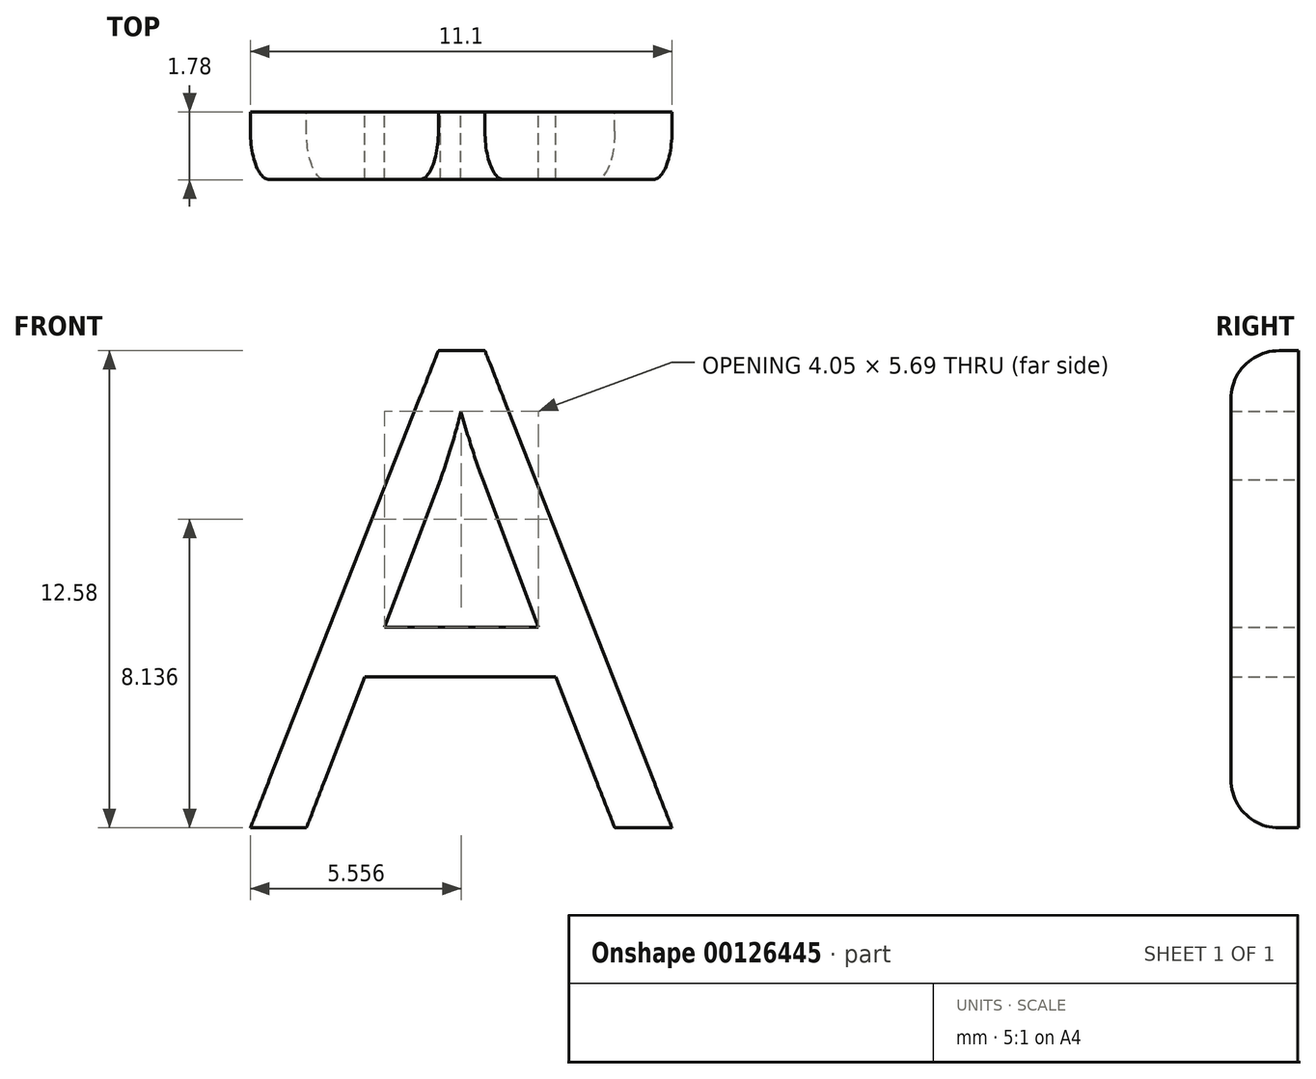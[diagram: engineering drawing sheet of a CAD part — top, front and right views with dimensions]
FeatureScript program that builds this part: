
annotation { "Feature Type Name" : "Feature", "Feature Type Description" : "" }
export const myFeature = defineFeature(function(context is Context, id is Id, definition is map)
    precondition{}
    {
        {
            var Q0;
            Q0=qCreatedBy(makeId("Front.planeOp"),FACE);
            var sketch = newSketch(context, id + "F0", { "sketchPlane" : qUnion([Q0])});
            skText(sketch, "E0", { "text": "A", "fontName": "OpenSans-Regular.ttf"});
            const initialGuessF0  = {"E0": [-0.00578, -0.00825, 1, 0, 0.01263]};
            skSetInitialGuess(sketch, initialGuessF0);
            skSolve(sketch);
        }
        {
            var Q0;
            Q0 = qSketchRegion(id + "F0", true);
            var Q1;
            Q1=makeQuery(id+"F0.imprint","IMPRINT",FACE,{"disambiguationData":[TD([[makeQuery(id+"F0.imprint","IMPRINT",EDGE,{"derivedFrom":sQuery(id+"F0.wireOp",EDGE,"E0.sketch_text.stroke-0")}),-1.0]])]});
            extrude(context, id + "F1", {"entities" : qUnion([Q0, Q1]), "depth" : 1.78 * mm});
        }
        {
            var Q0;
            Q0=makeQuery(id+"F1.opExtrude","CAP_EDGE",EDGE,{"disambiguationData":[OSD([sQuery(id+"F0.wireOp",EDGE,"E0.sketch_text.stroke-5")])],"isStart":false});
            var Q1;
            Q1=makeQuery(id+"F1.opExtrude","CAP_EDGE",EDGE,{"disambiguationData":[OSD([sQuery(id+"F0.wireOp",EDGE,"E0.sketch_text.stroke-3")])],"isStart":false});
            var Q2;
            Q2=makeQuery(id+"F1.opExtrude","CAP_EDGE",EDGE,{"disambiguationData":[OSD([sQuery(id+"F0.wireOp",EDGE,"E0.sketch_text.stroke-7")])],"isStart":false});
            fillet(context, id + "F2", {"entities" : qUnion([Q0, Q1, Q2]), "radius" : 1.27 * mm, "tangentPropagation" : true, "allowEdgeOverflow" : false});
        }
    });
